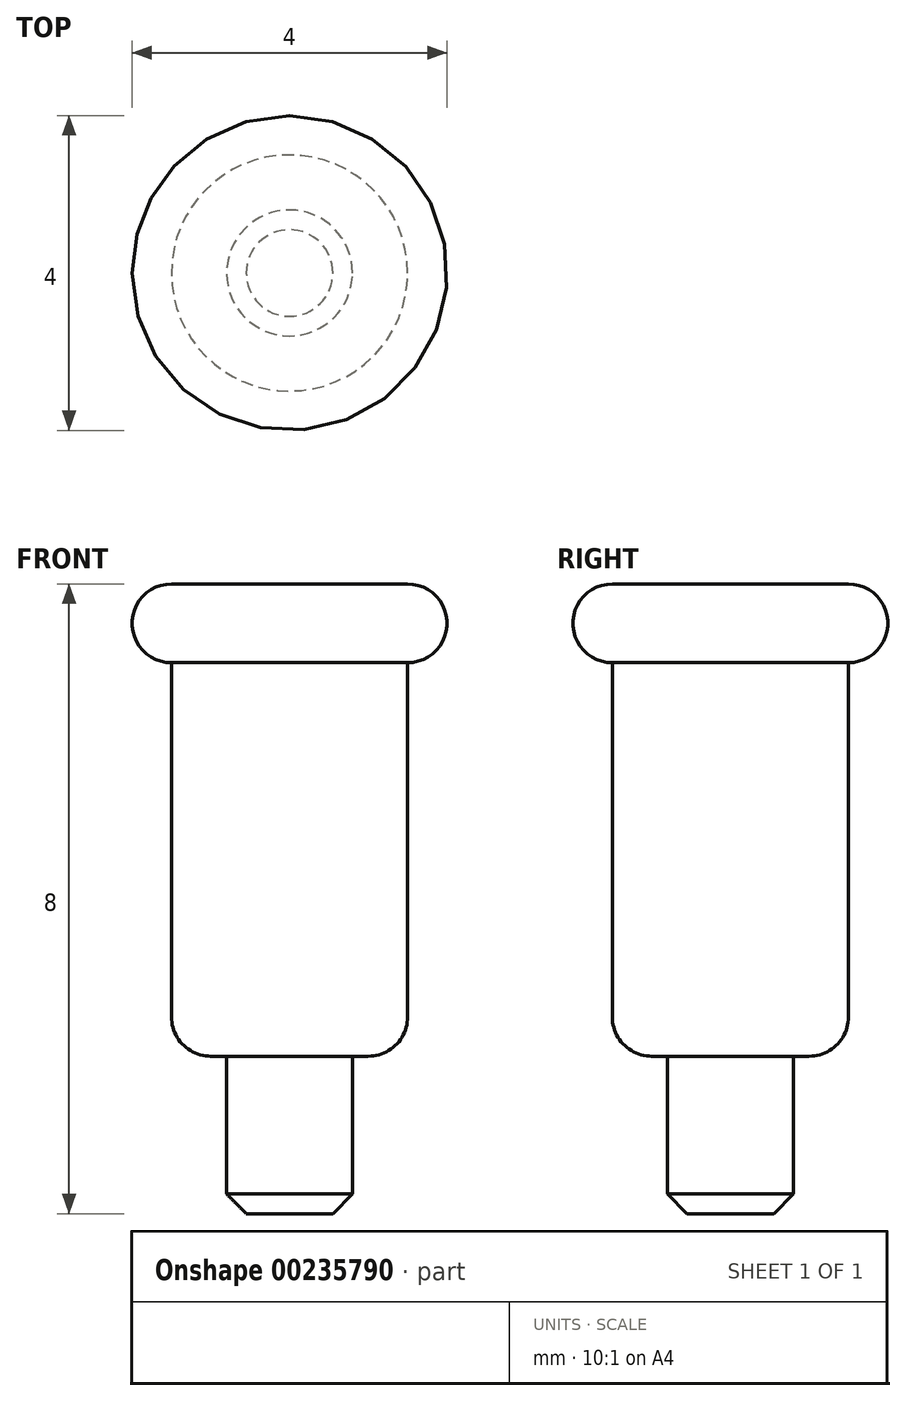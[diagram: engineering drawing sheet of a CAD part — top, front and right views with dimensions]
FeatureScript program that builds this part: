
annotation { "Feature Type Name" : "Feature", "Feature Type Description" : "" }
export const myFeature = defineFeature(function(context is Context, id is Id, definition is map)
    precondition{}
    {
        {
            var Q0;
            Q0=qCreatedBy(makeId("Front.planeOp"),FACE);
            var sketch = newSketch(context, id + "F0", { "sketchPlane" : qUnion([Q0])});
            skLineSegment(sketch, "E0", {"start": v(0, 0) * mm, "end": v(0, 4) * mm});
            skLineSegment(sketch, "E1.MirrorCS", {"start": v(0, 0) * mm, "end": v(0, -4) * mm});
            skLineSegment(sketch, "E2", {"start": v(0, 4) * mm, "end": v(1.5, 4) * mm});
            skLineSegment(sketch, "E3", {"start": v(0, 3) * mm, "end": v(1.5, 3) * mm});
            skArc(sketch, "E4", {"start": v(1.5, 3) * mm, "mid": v(2, 3.5) * mm, "end": v(1.5, 4) * mm});
            skLineSegment(sketch, "E5", {"start": v(0, -4) * mm, "end": v(0.8, -4) * mm});
            skLineSegment(sketch, "E6", {"start": v(1.5, 3) * mm, "end": v(1.5, -2) * mm});
            skLineSegment(sketch, "E7", {"start": v(0.8, -4) * mm, "end": v(0.8, -2) * mm});
            skLineSegment(sketch, "E8", {"start": v(0.8, -2) * mm, "end": v(1.5, -2) * mm});
            skSolve(sketch);
        }
        {
            var Q0;
            {var subQ0=sQuery(id+"F0.wireOp",EDGE,"E2");Q0=makeQuery(id+"F0.imprint","IMPRINT",FACE,{"disambiguationData":[TD([[makeQuery(id+"F0.imprint","IMPRINT",EDGE,{"derivedFrom":subQ0}),-1.0]])]});}
            var Q1;
            {var subQ1=sQuery(id+"F0.wireOp",EDGE,"E1.MirrorCS");Q1=makeQuery(id+"F0.imprint","IMPRINT",FACE,{"disambiguationData":[TD([[makeQuery(id+"F0.imprint","IMPRINT",EDGE,{"derivedFrom":subQ1}),1.0]])]});}
            var Q2;
            Q2=sQuery(id+"F0.wireOp",EDGE,"E0");
            revolve(context, id + "F1", {"entities" : qUnion([Q0, Q1]), "axis" : qUnion([Q2]), "revolveType" : RevolveType.FULL});
        }
        {
            var Q0;
            Q0=makeQuery(id+"F1.opRevolve","SWEPT_EDGE",EDGE,{"disambiguationData":[OSD([sQuery(id+"F0.wireOp",EDGE,"E6"),sQuery(id+"F0.wireOp",EDGE,"E8")])]});
            fillet(context, id + "F2", {"entities" : qUnion([Q0]), "radius" : .5 * mm, "tangentPropagation" : true, "allowEdgeOverflow" : false});
        }
        {
            var Q0;
            Q0=makeQuery(id+"F1.opRevolve","SWEPT_EDGE",EDGE,{"disambiguationData":[OSD([sQuery(id+"F0.wireOp",EDGE,"E5"),sQuery(id+"F0.wireOp",EDGE,"E7")])]});
            chamfer(context, id + "F3", {"entities" : qUnion([Q0]), "chamferType" : ChamferType.OFFSET_ANGLE, "width" : .25 * mm, "oppositeDirection" : false, "angle" : 45 * degree, "tangentPropagation" : true});
        }
    });
